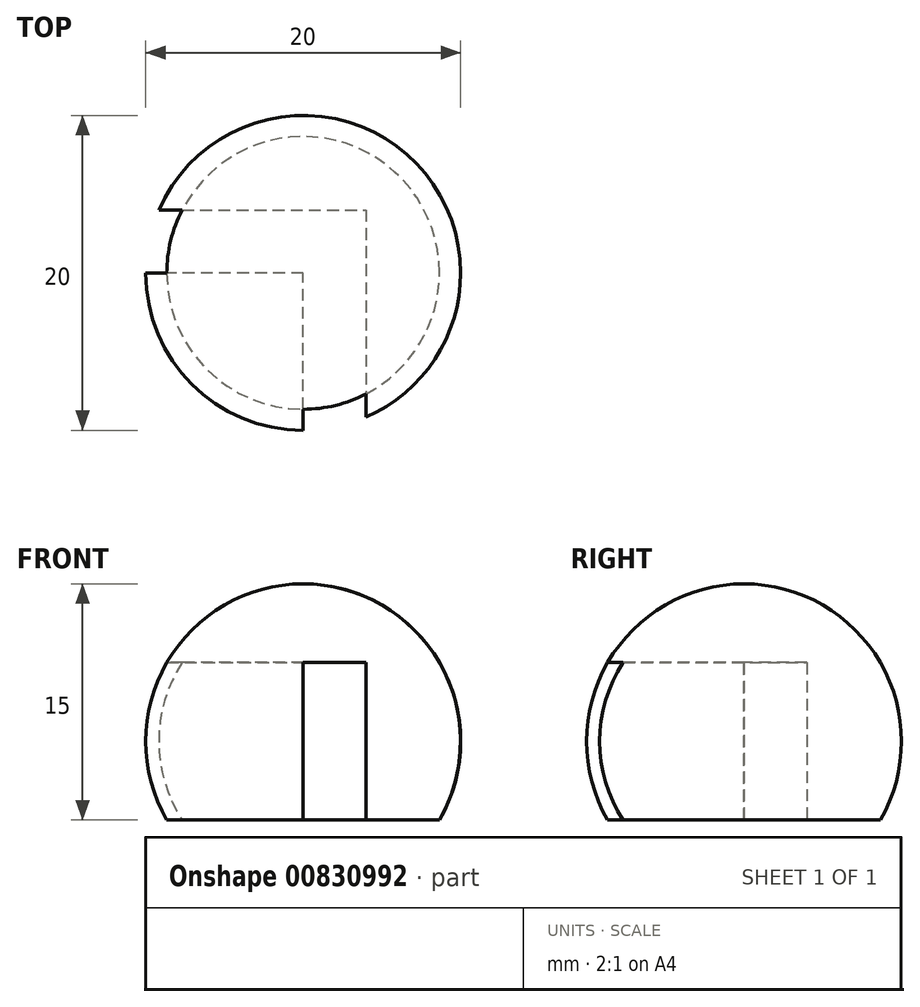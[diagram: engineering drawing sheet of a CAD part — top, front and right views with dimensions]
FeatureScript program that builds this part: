
annotation { "Feature Type Name" : "Feature", "Feature Type Description" : "" }
export const myFeature = defineFeature(function(context is Context, id is Id, definition is map)
    precondition{}
    {
        {
            var Q0;
            Q0=qCreatedBy(makeId("Front.planeOp"),FACE);
            var sketch = newSketch(context, id + "F0", { "sketchPlane" : qUnion([Q0])});
            skArc(sketch, "E0", {"start": v(0, -10) * mm, "mid": v(10, 0) * mm, "end": v(0, 10) * mm});
            skLineSegment(sketch, "E1", {"start": v(0, 10) * mm, "end": v(0, -10) * mm});
            skLineSegment(sketch, "E2", {"start": v(0, 11.58) * mm, "end": v(0, -13.45) * mm, "construction": true});
            skLineSegment(sketch, "E3", {"start": v(0, -5) * mm, "end": v(8.66, -5) * mm});
            skSolve(sketch);
        }
        {
            var Q0;
            {var subQ3=sQuery(id+"F0.wireOp",EDGE,"E3");Q0=makeQuery(id+"F0.imprint","IMPRINT",FACE,{"disambiguationData":[TD([[makeQuery(id+"F0.imprint","IMPRINT",EDGE,{"derivedFrom":subQ3}),1.0]])]});}
            var Q1;
            Q1=sQuery(id+"F0.wireOp",EDGE,"E2");
            revolve(context, id + "F1", {"surfaceOperationType" : NewSurfaceOperationType.NEW, "entities" : qUnion([Q0]), "axis" : qUnion([Q1]), "revolveType" : RevolveType.FULL});
        }
        {
            var Q0;
            Q0=qCreatedBy(makeId("Top.planeOp"),FACE);
            cPlane(context, id + "F2", {"entities" : qUnion([Q0]), "cplaneType" : CPlaneType.OFFSET, "offset" : 10 * mm, "oppositeDirection" : true, "width" : 150 * mm, "height" : 150 * mm});
        }
        {
            var Q0;
            Q0=qCreatedBy(id+"F2.planeOp",FACE);
            var sketch = newSketch(context, id + "F3", { "sketchPlane" : qUnion([Q0])});
            skLineSegment(sketch, "E4", {"start": v(-39.57, 0) * mm, "end": v(0, 0) * mm});
            skLineSegment(sketch, "E5", {"start": v(0, 0) * mm, "end": v(0, -35.4) * mm});
            skLineSegment(sketch, "E6", {"start": v(0, -35.4) * mm, "end": v(4, -35.4) * mm});
            skLineSegment(sketch, "E7", {"start": v(4, -35.4) * mm, "end": v(4, 4) * mm});
            skLineSegment(sketch, "E8", {"start": v(4, 4) * mm, "end": v(-39.57, 4) * mm});
            skLineSegment(sketch, "E9", {"start": v(-39.57, 4) * mm, "end": v(-39.57, 0) * mm});
            skSolve(sketch);
        }
        {
            var Q0;
            Q0 = qSketchRegion(id + "F3", true);
            extrude(context, id + "F4", {"entities" : qUnion([Q0]), "operationType" : NewBodyOperationType.REMOVE, "depth" : 15 * mm, "offsetDistance" : 25 * mm});
        }
    });
